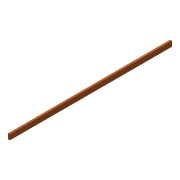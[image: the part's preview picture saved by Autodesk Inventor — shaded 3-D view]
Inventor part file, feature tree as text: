
AUTODESK INVENTOR PART (.ipt)
format: ipt  version: 2016 SP2 (Build 200236200, 236)  size: 94,208 bytes
history: native  units: in
note: dims shown in document units (in); Inventor stores cm internally (conversion verified against a paired STEP export)
features: sketch x3, extrude x1, hole x1
ambient origin geometry x8: Origin, YZ Plane, XZ Plane, XY Plane, X Axis, Y Axis, Z Axis, Center Point
bodies: Solid1 (feature_tree)
feature tree (5):
  extrude  "Extrusion1"  Depth=4.4882in
  hole  "Hole1"  [1 undecoded]
  sketch  "Sketch4"  dims[d13=0.1969in d14=0.75in d15=0.375in d16=0.25in d17=0.5635in d18=1.0in d19=0.8108in d22=1.122in]
  sketch  "Sketch1"  dims[d0=1.4961in d1=4.4882in]
  sketch  "Sketch2"  dims[d2=137.5984in d3=0.0in d6=0.7874in d8=2.2441in d9=0.3937in d11=1.0in]
note: 1 required parameter value undecoded (feature->parameter linkage not recoverable at this tier; creation-order binding heuristic only, values carry confidence <= 0.55)
